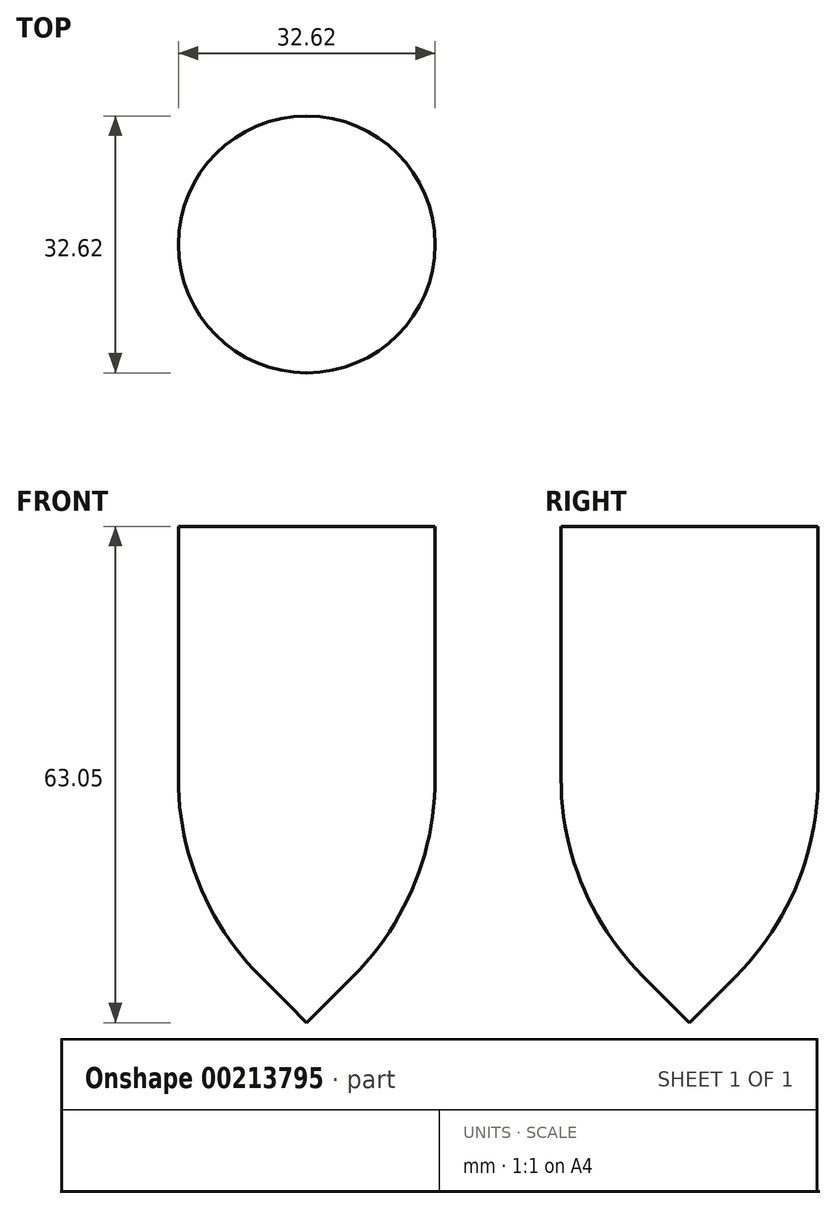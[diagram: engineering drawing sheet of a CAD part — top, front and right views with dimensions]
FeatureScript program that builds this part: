
annotation { "Feature Type Name" : "Feature", "Feature Type Description" : "" }
export const myFeature = defineFeature(function(context is Context, id is Id, definition is map)
    precondition{}
    {
        {
            var Q0;
            Q0=qCreatedBy(makeId("Top.planeOp"),FACE);
            var sketch = newSketch(context, id + "F0", { "sketchPlane" : qUnion([Q0])});
            skCircle(sketch, "E0", {"center": v(0, 0) * mm, "radius": 12.58 * mm});
            skSolve(sketch);
        }
        {
            var Q0;
            Q0=makeQuery(id+"F0.imprint","IMPRINT",FACE,{"disambiguationData":[TD([[makeQuery(id+"F0.imprint","IMPRINT",EDGE,{"derivedFrom":sQuery(id+"F0.wireOp",EDGE,"E0")}),1.0]])]});
            var sketch = newSketch(context, id + "F1", { "sketchPlane" : qUnion([Q0])});
            skCircle(sketch, "E1", {"center": v(0, 0) * mm, "radius": 16.31 * mm});
            skSolve(sketch);
        }
        {
            var Q0;
            Q0 = qSketchRegion(id + "F1", true);
            extrude(context, id + "F2", {"entities" : qUnion([Q0]), "depth" : 46.74 * mm});
        }
        {
            var Q0;
            Q0 = qSketchRegion(id + "F1", true);
            extrude(context, id + "F3", {"entities" : qUnion([Q0]), "operationType" : NewBodyOperationType.ADD, "oppositeDirection" : true, "depth" : 32.77 * mm, "hasDraft" : true, "draftAngle" : 45 * degree, "draftPullDirection" : true});
        }
        {
            var Q0;
            {var subQ0=sQuery(id+"F1.wireOp",EDGE,"E1");Q0=makeQuery(id+"F3.boolean.opBoolean","MERGE",EDGE,{"derivedFrom":[makeQuery(id+"F2.opExtrude","CAP_EDGE",EDGE,{"disambiguationData":[OSD([subQ0])],"isStart":true}),makeQuery(id+"F3.opExtrude","CAP_EDGE",EDGE,{"disambiguationData":[OSD([subQ0])],"isStart":true})]});}
            fillet(context, id + "F4", {"entities" : qUnion([Q0]), "radius" : 35.56 * mm, "tangentPropagation" : true, "allowEdgeOverflow" : false});
        }
    });
